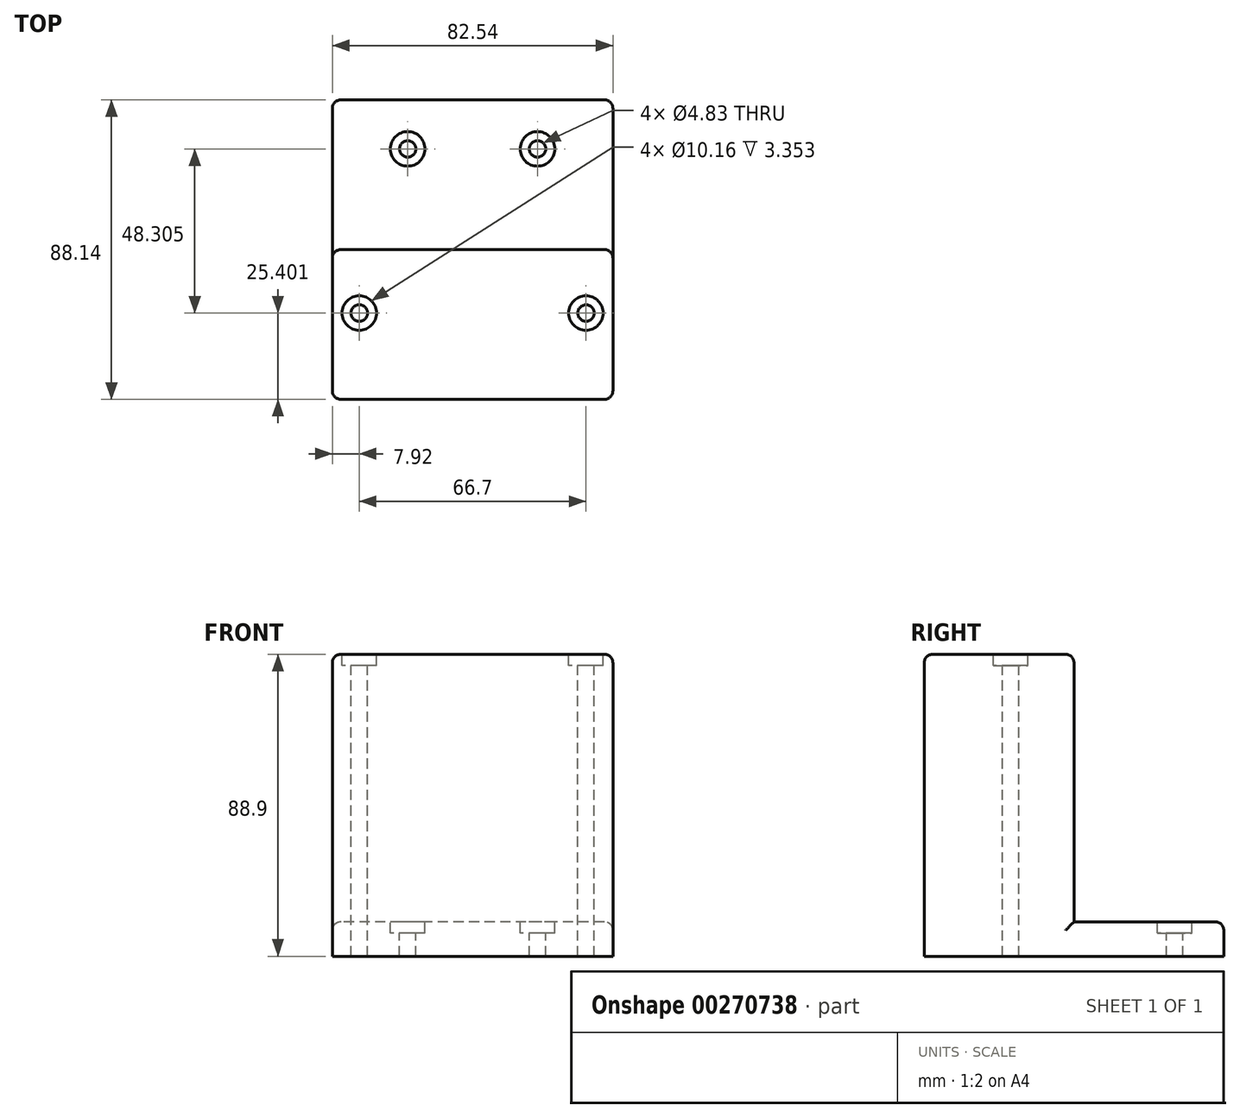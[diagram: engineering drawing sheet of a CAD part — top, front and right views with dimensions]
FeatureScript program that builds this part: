
annotation { "Feature Type Name" : "Feature", "Feature Type Description" : "" }
export const myFeature = defineFeature(function(context is Context, id is Id, definition is map)
    precondition{}
    {
        {
            var Q0;
            Q0=qCreatedBy(makeId("Front.planeOp"),FACE);
            var sketch = newSketch(context, id + "F0", { "sketchPlane" : qUnion([Q0])});
            skLineSegment(sketch, "E0.bottom", {"start": v(41.28, 44.45) * mm, "end": v(-41.28, 44.45) * mm});
            skLineSegment(sketch, "E0.top", {"start": v(41.27, -44.45) * mm, "end": v(-41.28, -44.45) * mm});
            skLineSegment(sketch, "E0.left", {"start": v(41.28, 44.45) * mm, "end": v(41.27, -44.45) * mm});
            skLineSegment(sketch, "E0.right", {"start": v(-41.28, 44.45) * mm, "end": v(-41.28, -44.45) * mm});
            skPoint(sketch, "E0.middle", {"position": v(0, 0) * mm});
            skSolve(sketch);
        }
        {
            var Q0;
            Q0 = qSketchRegion(id + "F0", true);
            extrude(context, id + "F1", {"entities" : qUnion([Q0]), "depth" : 44.07 * mm});
        }
        {
            var Q0;
            Q0=makeQuery(id+"F1.opExtrude","CAP_FACE",FACE,{"disambiguationData":[OSD([sQuery(id+"F0.wireOp",EDGE,"E0.bottom"),sQuery(id+"F0.wireOp",EDGE,"E0.top"),sQuery(id+"F0.wireOp",EDGE,"E0.left"),sQuery(id+"F0.wireOp",EDGE,"E0.right")])],"isStart":true});
            var sketch = newSketch(context, id + "F2", { "sketchPlane" : qUnion([Q0])});
            skLineSegment(sketch, "E1.bottom", {"start": v(-41.27, -44.45) * mm, "end": v(41.28, -44.45) * mm});
            skLineSegment(sketch, "E1.top", {"start": v(-41.27, -34.29) * mm, "end": v(41.28, -34.29) * mm});
            skLineSegment(sketch, "E1.left", {"start": v(-41.27, -44.45) * mm, "end": v(-41.27, -34.29) * mm});
            skLineSegment(sketch, "E1.right", {"start": v(41.28, -44.45) * mm, "end": v(41.28, -34.29) * mm});
            skSolve(sketch);
        }
        {
            var Q0;
            Q0 = qSketchRegion(id + "F2", true);
            extrude(context, id + "F3", {"entities" : qUnion([Q0]), "operationType" : NewBodyOperationType.ADD, "depth" : 44.07 * mm});
        }
        {
            var Q0;
            Q0=makeQuery(id+"F1.opExtrude","SWEPT_FACE",FACE,{"disambiguationData":[OSD([sQuery(id+"F0.wireOp",EDGE,"E0.bottom")])]});
            var sketch = newSketch(context, id + "F4", { "sketchPlane" : qUnion([Q0])});
            skLineSegment(sketch, "E2", {"start": v(0, -18.67) * mm, "end": v(-39.62, -18.67) * mm});
            skLineSegment(sketch, "E3", {"start": v(0, -18.67) * mm, "end": v(39.62, -18.67) * mm});
            skLineSegment(sketch, "E4", {"start": v(-39.62, -18.67) * mm, "end": v(-33.35, -18.67) * mm});
            skLineSegment(sketch, "E5", {"start": v(39.62, -18.67) * mm, "end": v(33.35, -18.67) * mm});
            skPoint(sketch, "E6", {"position": v(-33.35, -18.67) * mm});
            skPoint(sketch, "E7", {"position": v(33.35, -18.67) * mm});
            skSolve(sketch);
        }
        {
            var Q0;
            Q0=sQuery(id+"F4.wireOp",VERTEX,"E6");
            var Q1;
            Q1=sQuery(id+"F4.wireOp",VERTEX,"E7");
            var Q2;
            Q2=makeQuery(id+"F1.opExtrude","SWEPT_BODY",BODY,{"disambiguationData":[OSD([sQuery(id+"F0.wireOp",EDGE,"E0.bottom"),sQuery(id+"F0.wireOp",EDGE,"E0.top"),sQuery(id+"F0.wireOp",EDGE,"E0.left"),sQuery(id+"F0.wireOp",EDGE,"E0.right")])]});
            hole(context, id + "F5", {"style" : HoleStyle.C_BORE, "endStyle" : HoleEndStyle.THROUGH, "holeDiameter" : 4.83 * mm, "cBoreDiameter" : 10.16 * mm, "cBoreDepth" : 3.35 * mm, "tappedDepth" : 12.7 * mm, "tapClearance" : 3, "locations" : qUnion([Q0, Q1]), "scope" : qUnion([Q2])});
        }
        {
            var Q0;
            Q0=makeQuery(id+"F1.opExtrude","SWEPT_EDGE",EDGE,{"disambiguationData":[OSD([sQuery(id+"F0.wireOp",EDGE,"E0.bottom"),sQuery(id+"F0.wireOp",EDGE,"E0.right")])]});
            var Q1;
            Q1=makeQuery(id+"F1.opExtrude","SWEPT_EDGE",EDGE,{"disambiguationData":[OSD([sQuery(id+"F0.wireOp",EDGE,"E0.bottom"),sQuery(id+"F0.wireOp",EDGE,"E0.left")])]});
            var Q2;
            Q2=makeQuery(id+"F1.opExtrude","CAP_EDGE",EDGE,{"disambiguationData":[OSD([sQuery(id+"F0.wireOp",EDGE,"E0.bottom")])],"isStart":false});
            var Q3;
            Q3=makeQuery(id+"F1.opExtrude","CAP_EDGE",EDGE,{"disambiguationData":[OSD([sQuery(id+"F0.wireOp",EDGE,"E0.bottom")])],"isStart":true});
            var Q4;
            Q4=makeQuery(id+"F1.opExtrude","CAP_EDGE",EDGE,{"disambiguationData":[OSD([sQuery(id+"F0.wireOp",EDGE,"E0.left")])],"isStart":false});
            var Q5;
            Q5=makeQuery(id+"F1.opExtrude","CAP_EDGE",EDGE,{"disambiguationData":[OSD([sQuery(id+"F0.wireOp",EDGE,"E0.left")])],"isStart":true});
            var Q6;
            Q6=makeQuery(id+"F1.opExtrude","CAP_EDGE",EDGE,{"disambiguationData":[OSD([sQuery(id+"F0.wireOp",EDGE,"E0.right")])],"isStart":false});
            var Q7;
            Q7=makeQuery(id+"F1.opExtrude","CAP_EDGE",EDGE,{"disambiguationData":[OSD([sQuery(id+"F0.wireOp",EDGE,"E0.right")])],"isStart":true});
            var Q8;
            Q8=makeQuery(id+"F3.opExtrude","SWEPT_EDGE",EDGE,{"disambiguationData":[OSD([sQuery(id+"F0.wireOp",EDGE,"E0.right"),sQuery(id+"F2.wireOp",EDGE,"E1.top"),sQuery(id+"F2.wireOp",EDGE,"E1.right")])]});
            var Q9;
            Q9=makeQuery(id+"F3.opExtrude","CAP_EDGE",EDGE,{"disambiguationData":[OSD([sQuery(id+"F2.wireOp",EDGE,"E1.top")])],"isStart":false});
            var Q10;
            Q10=makeQuery(id+"F3.opExtrude","SWEPT_EDGE",EDGE,{"disambiguationData":[OSD([sQuery(id+"F0.wireOp",EDGE,"E0.left"),sQuery(id+"F2.wireOp",EDGE,"E1.top"),sQuery(id+"F2.wireOp",EDGE,"E1.left")])]});
            var Q11;
            Q11=makeQuery(id+"F3.opExtrude","CAP_EDGE",EDGE,{"disambiguationData":[OSD([sQuery(id+"F2.wireOp",EDGE,"E1.top")])],"isStart":true});
            var Q12;
            Q12=makeQuery(id+"F3.opExtrude","CAP_EDGE",EDGE,{"disambiguationData":[OSD([sQuery(id+"F2.wireOp",EDGE,"E1.left")])],"isStart":false});
            var Q13;
            Q13=makeQuery(id+"F3.opExtrude","CAP_EDGE",EDGE,{"disambiguationData":[OSD([sQuery(id+"F2.wireOp",EDGE,"E1.right")])],"isStart":false});
            fillet(context, id + "F6", {"entities" : qUnion([Q0, Q1, Q2, Q3, Q4, Q5, Q6, Q7, Q8, Q9, Q10, Q11, Q12, Q13]), "radius" : 2.54 * mm, "tangentPropagation" : true, "allowEdgeOverflow" : false});
        }
        {
            var Q0;
            Q0=makeQuery(id+"F3.opExtrude","SWEPT_FACE",FACE,{"disambiguationData":[OSD([sQuery(id+"F2.wireOp",EDGE,"E1.top")])]});
            var sketch = newSketch(context, id + "F7", { "sketchPlane" : qUnion([Q0])});
            skLineSegment(sketch, "E8", {"start": v(0, 29.64) * mm, "end": v(19.09, 29.64) * mm});
            skPoint(sketch, "E8.startSnap0", {"position": v(0, 2.54) * mm});
            skLineSegment(sketch, "E9", {"start": v(0, 29.64) * mm, "end": v(-19.1, 29.64) * mm});
            skPoint(sketch, "E10", {"position": v(-19.1, 29.64) * mm});
            skPoint(sketch, "E11", {"position": v(19.09, 29.64) * mm});
            skSolve(sketch);
        }
        {
            var Q0;
            Q0=sQuery(id+"F7.wireOp",VERTEX,"3d65942c-167b-4d60-b952-518eb0426d7d");
            var Q1;
            Q1=sQuery(id+"F7.wireOp",VERTEX,"d9bf8b0f-1c49-4f16-be80-a735f4d745e8");
            var Q2;
            Q2=sQuery(id+"F7.wireOp",VERTEX,"E10");
            var Q3;
            Q3=sQuery(id+"F7.wireOp",VERTEX,"E11");
            var Q4;
            Q4=makeQuery(id+"F1.opExtrude","SWEPT_BODY",BODY,{"disambiguationData":[OSD([sQuery(id+"F0.wireOp",EDGE,"E0.bottom"),sQuery(id+"F0.wireOp",EDGE,"E0.top"),sQuery(id+"F0.wireOp",EDGE,"E0.left"),sQuery(id+"F0.wireOp",EDGE,"E0.right")])]});
            hole(context, id + "F8", {"style" : HoleStyle.C_BORE, "endStyle" : HoleEndStyle.THROUGH, "holeDiameter" : 4.83 * mm, "cBoreDiameter" : 10.16 * mm, "cBoreDepth" : 3.35 * mm, "tappedDepth" : 12.7 * mm, "tapClearance" : 3, "locations" : qUnion([Q0, Q1, Q2, Q3]), "scope" : qUnion([Q4])});
        }
    });
